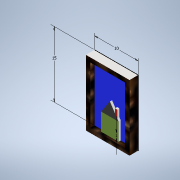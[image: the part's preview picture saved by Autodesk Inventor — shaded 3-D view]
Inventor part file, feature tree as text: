
AUTODESK INVENTOR PART (.ipt)
format: ipt  version: 2022 (Build 260153000, 153)  size: 155,136 bytes
history: native  units: mm
features: extrude x5, sketch x3
ambient origin geometry x8: Origin, YZ Plane, XZ Plane, XY Plane, X Axis, Y Axis, Z Axis, Center Point
bodies: Solid1 (feature_tree)
feature tree (8):
  sketch  "Sketch1"  dims[d0=10.0mm d1=15.0mm]
  extrude  "Extrusion1"  Depth=15.0mm
  sketch  "Sketch2"  dims[d2=1.0mm d3=1.0mm d4=0.0mm]
  extrude  "Extrusion2"  Depth=1.0mm TaperAngle=0.0deg
  sketch  "Sketch3"  dims[d5=2.0mm d6=0.0mm d7=4.0mm d8=4.0mm d9=2.0mm d10=3.0mm d11=1.0mm d12=0.5mm d13=0.5mm d14=0.0mm d15=0.499mm d16=0.0mm d17=0.498mm d18=0.0mm]
  extrude  "Extrusion3"  Depth=4.0mm
  extrude  "Extrusion4"  Depth=4.0mm
  extrude  "Extrusion5"  Depth=2.0mm
